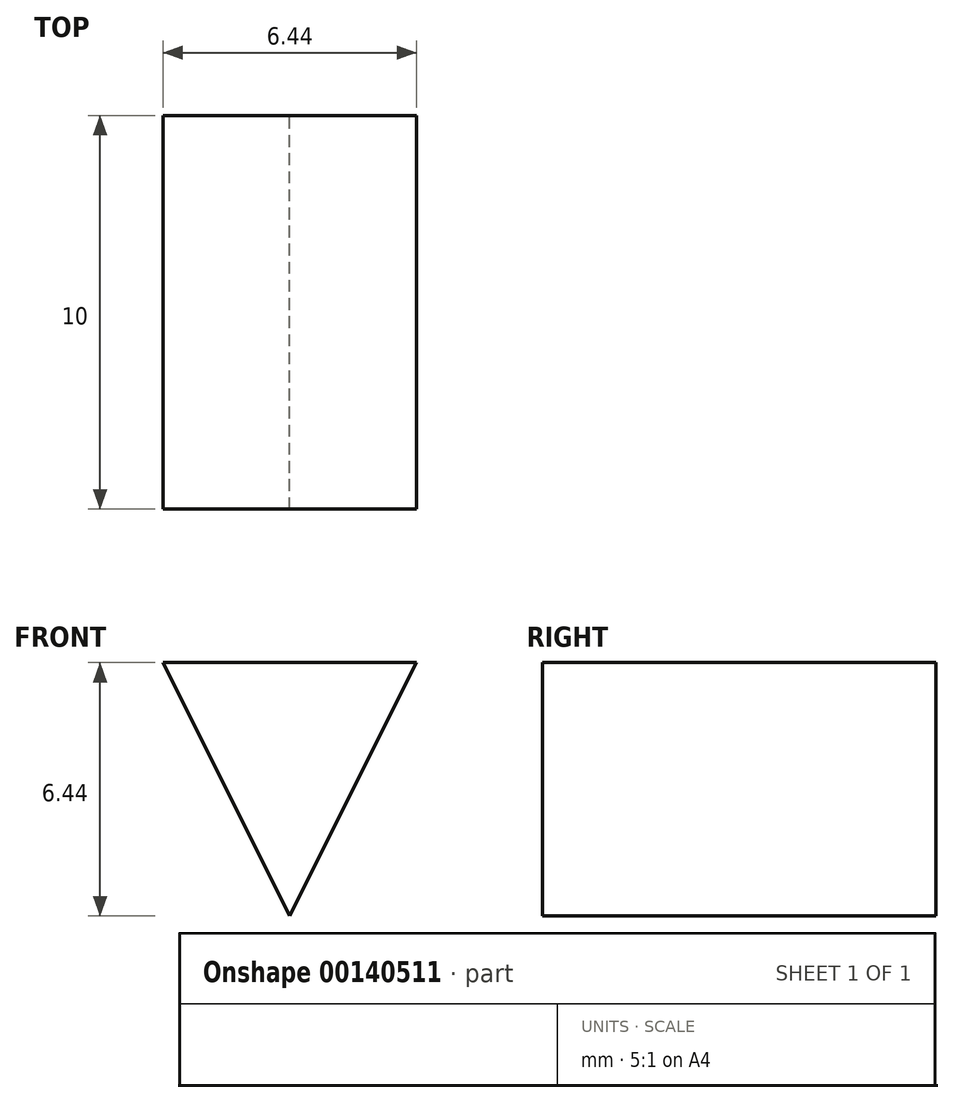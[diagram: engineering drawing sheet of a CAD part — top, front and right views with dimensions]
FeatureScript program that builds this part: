
annotation { "Feature Type Name" : "Feature", "Feature Type Description" : "" }
export const myFeature = defineFeature(function(context is Context, id is Id, definition is map)
    precondition{}
    {
        {
            var Q0;
            Q0=qCreatedBy(makeId("Front.planeOp"),FACE);
            var sketch = newSketch(context, id + "F0", { "sketchPlane" : qUnion([Q0])});
            skLineSegment(sketch, "E0", {"start": v(0, 0) * mm, "end": v(3.22, 0) * mm});
            skLineSegment(sketch, "E1", {"start": v(3.22, -6.44) * mm, "end": v(0, 0) * mm});
            skLineSegment(sketch, "E2", {"start": v(3.22, 0) * mm, "end": v(6.44, 0) * mm});
            skLineSegment(sketch, "E3", {"start": v(6.44, 0) * mm, "end": v(3.22, -6.44) * mm});
            skSolve(sketch);
        }
        {
            var Q0;
            Q0=makeQuery(id+"F0.imprint","IMPRINT",FACE,{"disambiguationData":[TD([[makeQuery(id+"F0.imprint","IMPRINT",EDGE,{"derivedFrom":sQuery(id+"F0.wireOp",EDGE,"E0")}),-1.0]])]});
            extrude(context, id + "F1", {"entities" : qUnion([Q0]), "depth" : 10 * mm});
        }
    });
